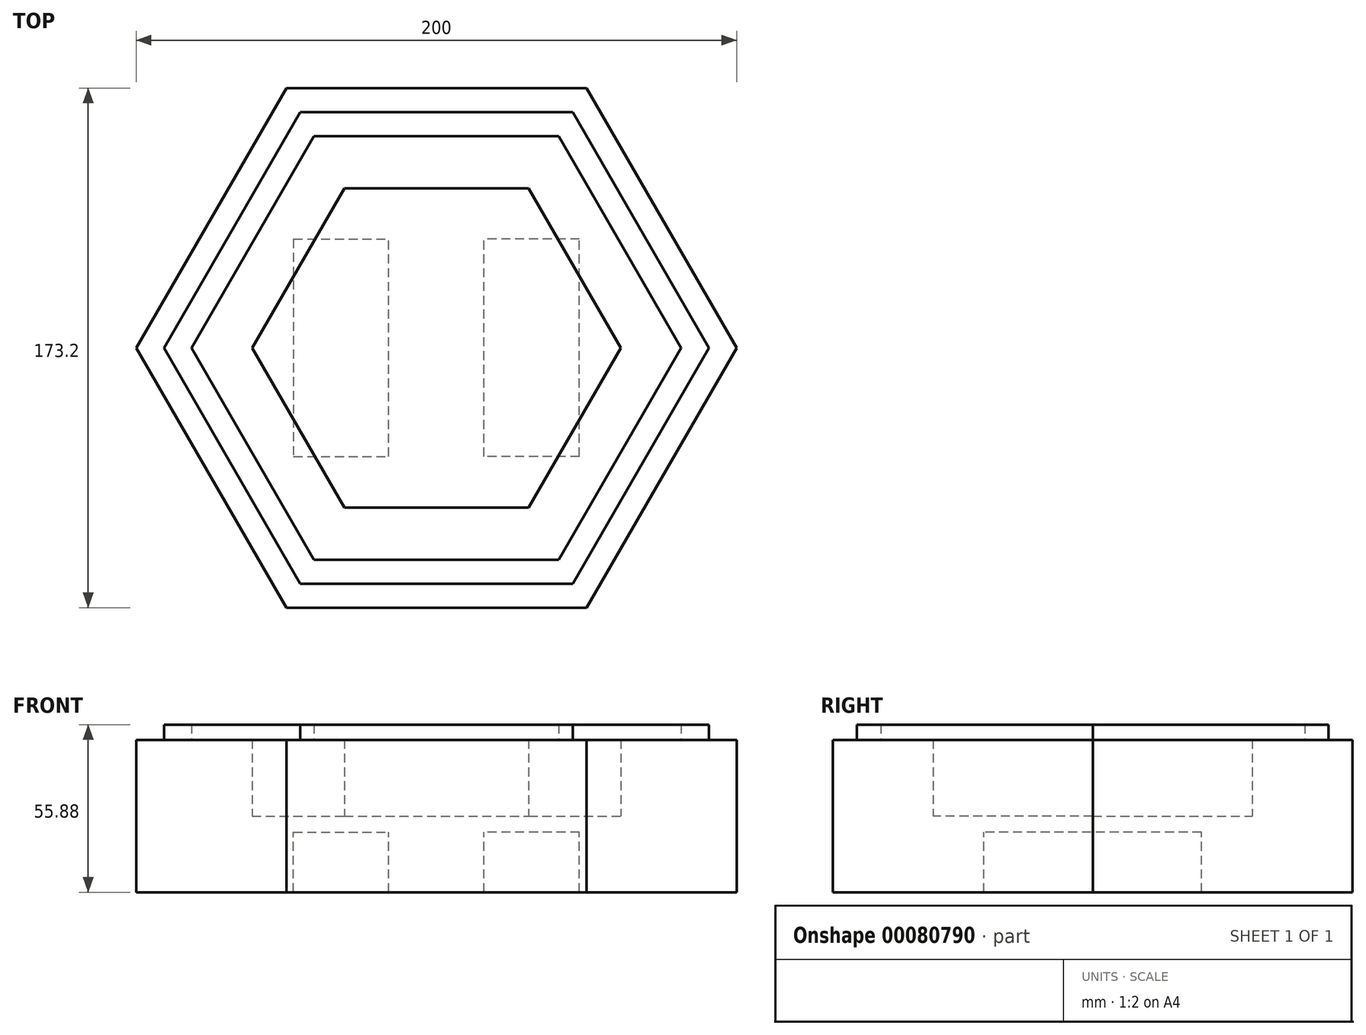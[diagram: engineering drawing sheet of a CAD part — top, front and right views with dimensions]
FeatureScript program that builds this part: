
annotation { "Feature Type Name" : "Feature", "Feature Type Description" : "" }
export const myFeature = defineFeature(function(context is Context, id is Id, definition is map)
    precondition{}
    {
        {
            var Q0;
            Q0=qCreatedBy(makeId("Top.planeOp"),FACE);
            var sketch = newSketch(context, id + "F0", { "sketchPlane" : qUnion([Q0])});
            skCircle(sketch, "E0.cCircle", {"center": v(0, 0) * mm, "radius": 70.6 * mm, "construction": true});
            skLineSegment(sketch, "E0.0", {"start": v(-40.76, 70.6) * mm, "end": v(40.76, 70.6) * mm});
            skLineSegment(sketch, "E0.1", {"start": v(40.76, 70.6) * mm, "end": v(81.52, 0) * mm});
            skLineSegment(sketch, "E0.2", {"start": v(81.52, 0) * mm, "end": v(40.76, -70.6) * mm});
            skLineSegment(sketch, "E0.3", {"start": v(40.76, -70.6) * mm, "end": v(-40.76, -70.6) * mm});
            skLineSegment(sketch, "E0.4", {"start": v(-40.76, -70.6) * mm, "end": v(-81.52, 0) * mm});
            skLineSegment(sketch, "E0.5", {"start": v(-81.52, 0) * mm, "end": v(-40.76, 70.6) * mm});
            skPoint(sketch, "E0.0.midPoint", {"position": v(0, 70.6) * mm});
            skLineSegment(sketch, "E1.0", {"start": v(-90.76, 0) * mm, "end": v(-45.38, 78.6) * mm});
            skLineSegment(sketch, "E1.1", {"start": v(45.38, 78.6) * mm, "end": v(90.76, 0) * mm});
            skLineSegment(sketch, "E1.2", {"start": v(90.76, 0) * mm, "end": v(45.38, -78.6) * mm});
            skLineSegment(sketch, "E1.3", {"start": v(-45.38, 78.6) * mm, "end": v(45.38, 78.6) * mm});
            skLineSegment(sketch, "E1.4", {"start": v(45.38, -78.6) * mm, "end": v(-45.38, -78.6) * mm});
            skLineSegment(sketch, "E1.5", {"start": v(-45.38, -78.6) * mm, "end": v(-90.76, 0) * mm});
            skLineSegment(sketch, "E2.0", {"start": v(50, -86.6) * mm, "end": v(-50, -86.6) * mm});
            skLineSegment(sketch, "E2.1", {"start": v(-100, 0) * mm, "end": v(-50, 86.6) * mm});
            skLineSegment(sketch, "E2.2", {"start": v(-50, 86.6) * mm, "end": v(50, 86.6) * mm});
            skLineSegment(sketch, "E2.3", {"start": v(-50, -86.6) * mm, "end": v(-100, 0) * mm});
            skLineSegment(sketch, "E2.4", {"start": v(50, 86.6) * mm, "end": v(100, 0) * mm});
            skLineSegment(sketch, "E2.5", {"start": v(100, 0) * mm, "end": v(50, -86.6) * mm});
            skSolve(sketch);
        }
        {
            var Q0;
            Q0=makeQuery(id+"F0.imprint","IMPRINT",FACE,{"disambiguationData":[TD([[makeQuery(id+"F0.imprint","IMPRINT",EDGE,{"derivedFrom":sQuery(id+"F0.wireOp",EDGE,"E0.0")}),1.0]])]});
            var Q1;
            Q1=makeQuery(id+"F0.imprint","IMPRINT",FACE,{"disambiguationData":[TD([[makeQuery(id+"F0.imprint","IMPRINT",EDGE,{"derivedFrom":sQuery(id+"F0.wireOp",EDGE,"E1.0")}),1.0]])]});
            extrude(context, id + "F1", {"entities" : qUnion([Q0, Q1]), "depth" : 50.8 * mm});
        }
        {
            var Q0;
            Q0=makeQuery(id+"F0.imprint","IMPRINT",FACE,{"disambiguationData":[TD([[makeQuery(id+"F0.imprint","IMPRINT",EDGE,{"derivedFrom":sQuery(id+"F0.wireOp",EDGE,"E0.0")}),1.0]])]});
            extrude(context, id + "F2", {"entities" : qUnion([Q0]), "operationType" : NewBodyOperationType.ADD, "depth" : 55.88 * mm});
        }
        {
            var Q0;
            Q0=makeQuery(id+"F0.imprint","IMPRINT",FACE,{"disambiguationData":[TD([[makeQuery(id+"F0.imprint","IMPRINT",EDGE,{"derivedFrom":sQuery(id+"F0.wireOp",EDGE,"E0.0")}),-1.0]])]});
            extrude(context, id + "F3", {"entities" : qUnion([Q0]), "operationType" : NewBodyOperationType.ADD, "depth" : 50.8 * mm});
        }
        {
            var Q0;
            Q0=makeQuery(id+"F3.opExtrude","CAP_FACE",FACE,{"disambiguationData":[OSD([sQuery(id+"F0.wireOp",EDGE,"E0.0"),sQuery(id+"F0.wireOp",EDGE,"E0.1"),sQuery(id+"F0.wireOp",EDGE,"E0.2"),sQuery(id+"F0.wireOp",EDGE,"E0.3"),sQuery(id+"F0.wireOp",EDGE,"E0.4"),sQuery(id+"F0.wireOp",EDGE,"E0.5")])],"isStart":false});
            shell(context, id + "F4", {"entities" : qUnion([Q0]), "thickness" : 25.4 * mm});
        }
        {
            var Q0;
            Q0=makeQuery(id+"F0.imprint","IMPRINT",FACE,{"disambiguationData":[TD([[makeQuery(id+"F0.imprint","IMPRINT",EDGE,{"derivedFrom":sQuery(id+"F0.wireOp",EDGE,"E0.0")}),-1.0]])]});
            var sketch = newSketch(context, id + "F5", { "sketchPlane" : qUnion([Q0])});
            skLineSegment(sketch, "E3", {"start": v(-47.63, 36.25) * mm, "end": v(-15.88, 36.25) * mm});
            skLineSegment(sketch, "E4", {"start": v(-47.62, 36.25) * mm, "end": v(-47.62, 0) * mm});
            skLineSegment(sketch, "E5.MirrorCS", {"start": v(-47.62, -36.25) * mm, "end": v(-47.63, 0) * mm});
            skLineSegment(sketch, "E6.MirrorCS", {"start": v(-47.63, -36.25) * mm, "end": v(-15.88, -36.25) * mm});
            skLineSegment(sketch, "E7", {"start": v(-15.88, -36.25) * mm, "end": v(-15.87, 36.25) * mm});
            skLineSegment(sketch, "E8.MirrorCS", {"start": v(15.87, -36.25) * mm, "end": v(15.88, 36.25) * mm});
            skLineSegment(sketch, "E9.MirrorCS", {"start": v(47.63, -36.25) * mm, "end": v(15.88, -36.25) * mm});
            skLineSegment(sketch, "E10.MirrorCS", {"start": v(47.62, -36.25) * mm, "end": v(47.62, 0) * mm});
            skLineSegment(sketch, "E11.MirrorCS", {"start": v(47.62, 36.25) * mm, "end": v(47.62, 0) * mm});
            skLineSegment(sketch, "E12.MirrorCS", {"start": v(47.63, 36.25) * mm, "end": v(15.88, 36.25) * mm});
            skSolve(sketch);
        }
        {
            var Q0;
            Q0=makeQuery(id+"F0.imprint","IMPRINT",FACE,{"disambiguationData":[TD([[makeQuery(id+"F0.imprint","IMPRINT",EDGE,{"derivedFrom":sQuery(id+"F0.wireOp",EDGE,"E0.0")}),-1.0]])]});
            var Q1;
            {var subQ8=sQuery(id+"F5.wireOp",EDGE,"E8.MirrorCS");Q1=makeQuery(id+"F5.imprint","IMPRINT",FACE,{"disambiguationData":[TD([[makeQuery(id+"F5.imprint","IMPRINT",EDGE,{"derivedFrom":subQ8}),-1.0]])]});}
            extrude(context, id + "F6", {"entities" : qUnion([Q0, Q1]), "operationType" : NewBodyOperationType.REMOVE, "oppositeDirection" : true, "depth" : 50.8 * mm});
        }
        {
            var Q0;
            Q0=makeQuery(id+"F5.imprint","IMPRINT",FACE,{"disambiguationData":[TD([[makeQuery(id+"F5.imprint","IMPRINT",EDGE,{"derivedFrom":sQuery(id+"F5.wireOp",EDGE,"E8.MirrorCS")}),-1.0]])]});
            var Q1;
            Q1=makeQuery(id+"F5.imprint","IMPRINT",FACE,{"disambiguationData":[TD([[makeQuery(id+"F5.imprint","IMPRINT",EDGE,{"derivedFrom":sQuery(id+"F5.wireOp",EDGE,"E3")}),-1.0]])]});
            extrude(context, id + "F7", {"entities" : qUnion([Q0, Q1]), "operationType" : NewBodyOperationType.REMOVE, "oppositeDirection" : true, "depth" : 40 * mm, "symmetric" : true});
        }
        {
            var Q0;
            Q0=makeQuery(id+"F1.opExtrude","SWEPT_BODY",BODY,{"disambiguationData":[OSD([sQuery(id+"F0.wireOp",EDGE,"E0.0"),sQuery(id+"F0.wireOp",EDGE,"E0.1"),sQuery(id+"F0.wireOp",EDGE,"E0.2"),sQuery(id+"F0.wireOp",EDGE,"E0.3"),sQuery(id+"F0.wireOp",EDGE,"E0.4"),sQuery(id+"F0.wireOp",EDGE,"E0.5"),sQuery(id+"F0.wireOp",EDGE,"E2.0"),sQuery(id+"F0.wireOp",EDGE,"E2.1"),sQuery(id+"F0.wireOp",EDGE,"E2.2"),sQuery(id+"F0.wireOp",EDGE,"E2.3"),sQuery(id+"F0.wireOp",EDGE,"E2.4"),sQuery(id+"F0.wireOp",EDGE,"E2.5")])]});
            var Q1;
            Q1=makeQuery(id+"F4.opShell","TWEAK_EDGE",EDGE,{"derivedFrom":[makeQuery(id+"F2.opExtrude","SWEPT_FACE",FACE,{"disambiguationData":[OSD([sQuery(id+"F0.wireOp",EDGE,"E1.5")])]}),makeQuery(id+"F3.opExtrude","CAP_FACE",FACE,{"disambiguationData":[OSD([sQuery(id+"F0.wireOp",EDGE,"E0.0"),sQuery(id+"F0.wireOp",EDGE,"E0.1"),sQuery(id+"F0.wireOp",EDGE,"E0.2"),sQuery(id+"F0.wireOp",EDGE,"E0.3"),sQuery(id+"F0.wireOp",EDGE,"E0.4"),sQuery(id+"F0.wireOp",EDGE,"E0.5")])],"isStart":false})]});
            circularPattern(context, id + "F8", {"entities" : qUnion([Q0]), "axis" : qUnion([Q1]), "angle" : 30 * degree, "instanceCount" : 2});
        }
        {
            var Q0;
            Q0=makeQuery(id+"F8.opPattern","COPY",BODY,{"derivedFrom":makeQuery(id+"F1.opExtrude","SWEPT_BODY",BODY,{"disambiguationData":[OSD([sQuery(id+"F0.wireOp",EDGE,"E0.0"),sQuery(id+"F0.wireOp",EDGE,"E0.1"),sQuery(id+"F0.wireOp",EDGE,"E0.2"),sQuery(id+"F0.wireOp",EDGE,"E0.3"),sQuery(id+"F0.wireOp",EDGE,"E0.4"),sQuery(id+"F0.wireOp",EDGE,"E0.5"),sQuery(id+"F0.wireOp",EDGE,"E2.0"),sQuery(id+"F0.wireOp",EDGE,"E2.1"),sQuery(id+"F0.wireOp",EDGE,"E2.2"),sQuery(id+"F0.wireOp",EDGE,"E2.3"),sQuery(id+"F0.wireOp",EDGE,"E2.4"),sQuery(id+"F0.wireOp",EDGE,"E2.5")])]}),"instanceName":"1"});
            deleteBodies(context, id + "F9", {"entities" : qUnion([Q0])});
        }
    });
